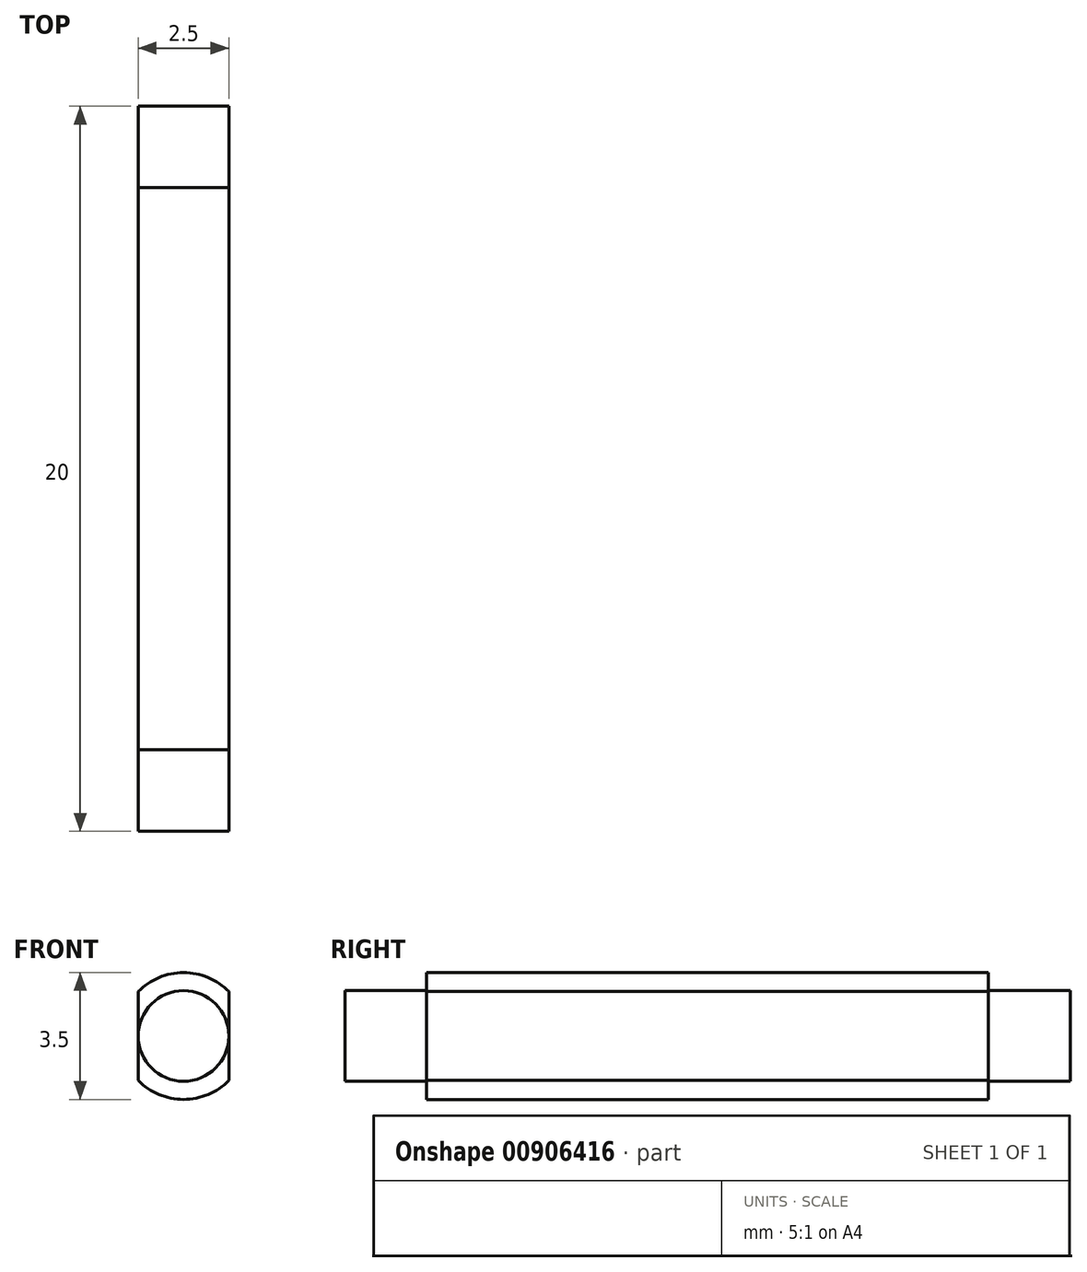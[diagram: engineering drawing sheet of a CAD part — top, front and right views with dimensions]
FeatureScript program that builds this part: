
annotation { "Feature Type Name" : "Feature", "Feature Type Description" : "" }
export const myFeature = defineFeature(function(context is Context, id is Id, definition is map)
    precondition{}
    {
        {
            var Q0;
            Q0=qCreatedBy(makeId("Front.planeOp"),FACE);
            var sketch = newSketch(context, id + "F0", { "sketchPlane" : qUnion([Q0])});
            skArc(sketch, "E0", {"start": v(-1.25, -1.22) * mm, "mid": v(0, -1.75) * mm, "end": v(1.25, -1.22) * mm});
            skLineSegment(sketch, "E1", {"start": v(-1.25, 1.22) * mm, "end": v(-1.25, -1.22) * mm});
            skLineSegment(sketch, "E2", {"start": v(1.25, 1.22) * mm, "end": v(1.25, -1.22) * mm});
            skArc(sketch, "E3.trimOffspring", {"start": v(1.25, 1.22) * mm, "mid": v(0, 1.75) * mm, "end": v(-1.25, 1.22) * mm});
            skSolve(sketch);
        }
        {
            var Q0;
            Q0=qSketchRegion(id+"F0",true);
            extrude(context, id + "F1", {"entities" : qUnion([Q0]), "endBound" : BoundingType.SYMMETRIC, "depth" : 15.5 * mm, "offsetDistance" : 25 * mm});
        }
        {
            var Q0;
            Q0=qCreatedBy(makeId("Front.planeOp"),FACE);
            var sketch = newSketch(context, id + "F2", { "sketchPlane" : qUnion([Q0])});
            skCircle(sketch, "E4", {"center": v(0, 0) * mm, "radius": 1.25 * mm});
            skSolve(sketch);
        }
        {
            var Q0;
            Q0=qSketchRegion(id+"F2",true);
            extrude(context, id + "F3", {"entities" : qUnion([Q0]), "operationType" : NewBodyOperationType.ADD, "endBound" : BoundingType.SYMMETRIC, "depth" : 20 * mm, "offsetDistance" : 25 * mm});
        }
    });
